# Revit family: NLRS_57_DUA_UN_Rectangular_Attenuator_LT_AGC_Solid_Air
name_source: partatom
category: Duct Accessories
revit_build: Autodesk Revit 2017 (Build: 20190508_0315(x64)
units: mm (PartAtom-declared; Revit-internal decimal feet)

## family parameters
Always vertical = Yes
Cut with Voids When Loaded = No
Part Type = Breaks Into
Round Connector Dimension = Use Diameter
Shared = No
Work Plane-Based = No

## types (4) — shared parameters
Assembly Code = 57.70
Code = AGC_Article_Codes
Description = Rechthoekige geluiddemper
Generic_Name = AGC_Article_Data_Generic
Manufacturer = Solid Air Climate Solutions
Model = Geluiddemper - Rechthoekig
NLRS_C_content_datum_uitgifte = 24-01-2020
NLRS_C_content_provider = Solid Air Climate Systems
NLRS_C_content_versie = Versie 1.7
NLRS_C_description = Rechthoekige geluiddemper
NLRS_C_niveau ontwikkeling = LOD400
SACS_AX_Prefix = 935
SACS_Dummy = 1
data = AGC_Article_Data

## per-type parameters (varying)
| type | Baffle_Type | Baffle_Width | Type Comments |
| AGCWR | 2 | 100 mm  [stored 0.328084 ft] | Check flow direction! |
| AGCXR | 2 | 200 mm  [stored 0.656168 ft] | Check flow direction! |
| AGCWA | 1 | 100 mm  [stored 0.328084 ft] |  |
| AGCXA | 1 | 200 mm  [stored 0.656168 ft] | Check flow direction! |

note: [stored X ft] marks values corroborated as IEEE doubles in the binary element streams (Revit-internal decimal feet)

## geometry (parser evidence)
native form markers: Sweep x8
no freeform markers — native parametric forms only
